# Revit family: PRD_AR_EyeWshFntns_EyeShower_FAID103
name_source: partatom
category: Plumbing Fixtures
revit_build: Autodesk Revit 2018 (Build: 20190510_1515(x64)
units: mm (PartAtom-declared; Revit-internal decimal feet)

## family parameters
Cut with Voids When Loaded = Yes
Host = Face
OmniClass Number = 23.45.05.14.24
OmniClass Title = Eye Wash Fountains
Part Type = Normal
Room Calculation Point = No
Round Connector Dimension = Use Diameter
Shared = Yes

## types (1)
- FAID103
    AssetType = Fixed
    BIMObjectName = PRD_AR_EyeWashingFountains_EyeShower_FAID103
    Category = Pr_40_20_27_28, Eye-wash fountains
    Color = green
    Default Elevation = 925 mm  [stored 3.03478 ft]
    Description = Eye-wash and face-wash fountain with green plastic hand shower and hose with a stainless steel cover. Meets the requirements of EN 15154, Part -2. Green plastic hand shower, dust protection cap with user instructions.
    DiameterNominal = 15  [stored 0.0492126 ft]
    DrainSize = 15 mm  [stored 0.0492126 ft]
    DripPan = No
    DurationUnit = year
    Features = for mounting on walls or laboratory furniture, with spiral hose
    FittingMaterial = PRD_AR_Plastic_White
    GrossWeight = 1.35 kg
    HandShowerMaterial = PRD_AR_Plastic_Green
    HasTray = FALSE
    HoseMaterial = PRD_AR_StainlessSteel_SatinFinished
    IfcExportAs = IfcSanitaryTerminalType
    IfcExportType = SHOWER
    InletSize = DN 15
    Manufacturer = KWC Group AG
    ManufacturerName = KWC Group AG
    ManufacturerURL = www.kwc.com
    Material = plastic
    Model = FAID103
    ModelNumber = 2000101102
    ModelReference = FAID103
    NBSDescription = Wash fountain packages
    NBSReference = 45-35-70/406
    Name = Eye Shower FAID103
    NetWeight = 1.01 kg
    NominalDepth = 0 mm  [stored 0 ft]
    NominalHeight = 0 mm  [stored 0 ft]
    NominalWidth = 0 mm  [stored 0 ft]
    ProductInformation = https://pim.kwc.com
    ShowerType = Individual
    TypeOfFitting = Laboratory furniture
    TypeOfOperation = Trigger button
    URL = www.kwc.com
    Uniclass2015Code = Pr_40_20_27_28
    Uniclass2015Title = Eye-wash fountains
    Uniclass2015Version = Products v1.17
    Version = 1
    WarrantyDurationUnit = year

note: [stored X ft] marks values corroborated as IEEE doubles in the binary element streams (Revit-internal decimal feet)

## geometry (parser evidence)
native form markers: Sweep x6
no freeform markers — native parametric forms only
